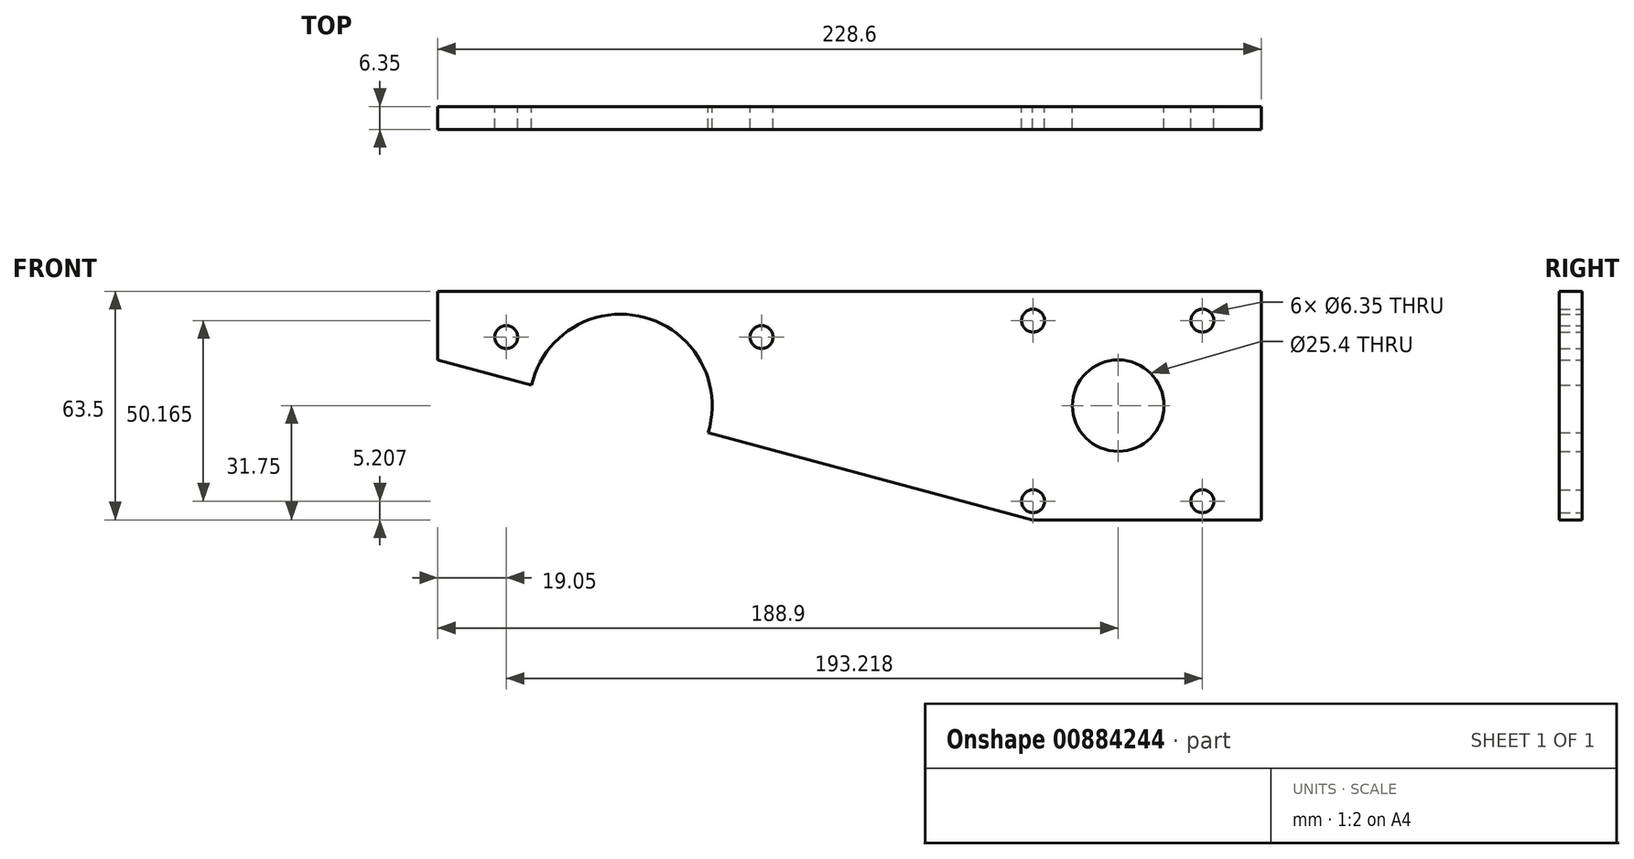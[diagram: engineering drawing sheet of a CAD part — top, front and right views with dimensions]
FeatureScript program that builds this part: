
annotation { "Feature Type Name" : "Feature", "Feature Type Description" : "" }
export const myFeature = defineFeature(function(context is Context, id is Id, definition is map)
    precondition{}
    {
        {
            var Q0;
            Q0=qCreatedBy(makeId("Front.planeOp"),FACE);
            var sketch = newSketch(context, id + "F0", { "sketchPlane" : qUnion([Q0])});
            skCircle(sketch, "E0", {"center": v(-31.75, 19.05) * mm, "radius": 3.18 * mm});
            skCircle(sketch, "E1", {"center": v(39.12, 19.05) * mm, "radius": 3.18 * mm});
            skCircle(sketch, "E2", {"center": v(138.1, 0) * mm, "radius": 12.7 * mm});
            skCircle(sketch, "E3", {"center": v(114.48, 23.62) * mm, "radius": 3.18 * mm});
            skCircle(sketch, "E4", {"center": v(161.47, 23.62) * mm, "radius": 3.18 * mm});
            skCircle(sketch, "E5", {"center": v(161.47, -26.54) * mm, "radius": 3.18 * mm});
            skCircle(sketch, "E6", {"center": v(114.48, -26.54) * mm, "radius": 3.17 * mm});
            skLineSegment(sketch, "E7.bottom", {"start": v(-50.8, 31.75) * mm, "end": v(177.8, 31.75) * mm});
            skLineSegment(sketch, "E7.top", {"start": v(114.3, -31.75) * mm, "end": v(177.8, -31.75) * mm});
            skLineSegment(sketch, "E7.left", {"start": v(-50.8, 31.75) * mm, "end": v(-50.8, 12.7) * mm});
            skLineSegment(sketch, "E7.right", {"start": v(177.8, 31.75) * mm, "end": v(177.8, -31.75) * mm});
            skLineSegment(sketch, "E8", {"start": v(-50.8, 12.7) * mm, "end": v(-24.75, 5.69) * mm});
            skArc(sketch, "E9", {"start": v(24.26, -7.5) * mm, "mid": v(6.6, 24.53) * mm, "end": v(-24.75, 5.69) * mm});
            skLineSegment(sketch, "E10.trimOffspring", {"start": v(24.26, -7.5) * mm, "end": v(114.3, -31.75) * mm});
            skSolve(sketch);
        }
        {
            var Q0;
            Q0 = qSketchRegion(id + "F0", true);
            extrude(context, id + "F1", {"entities" : qUnion([Q0]), "depth" : 6.35 * mm, "offsetDistance" : 25.4 * mm});
        }
    });
